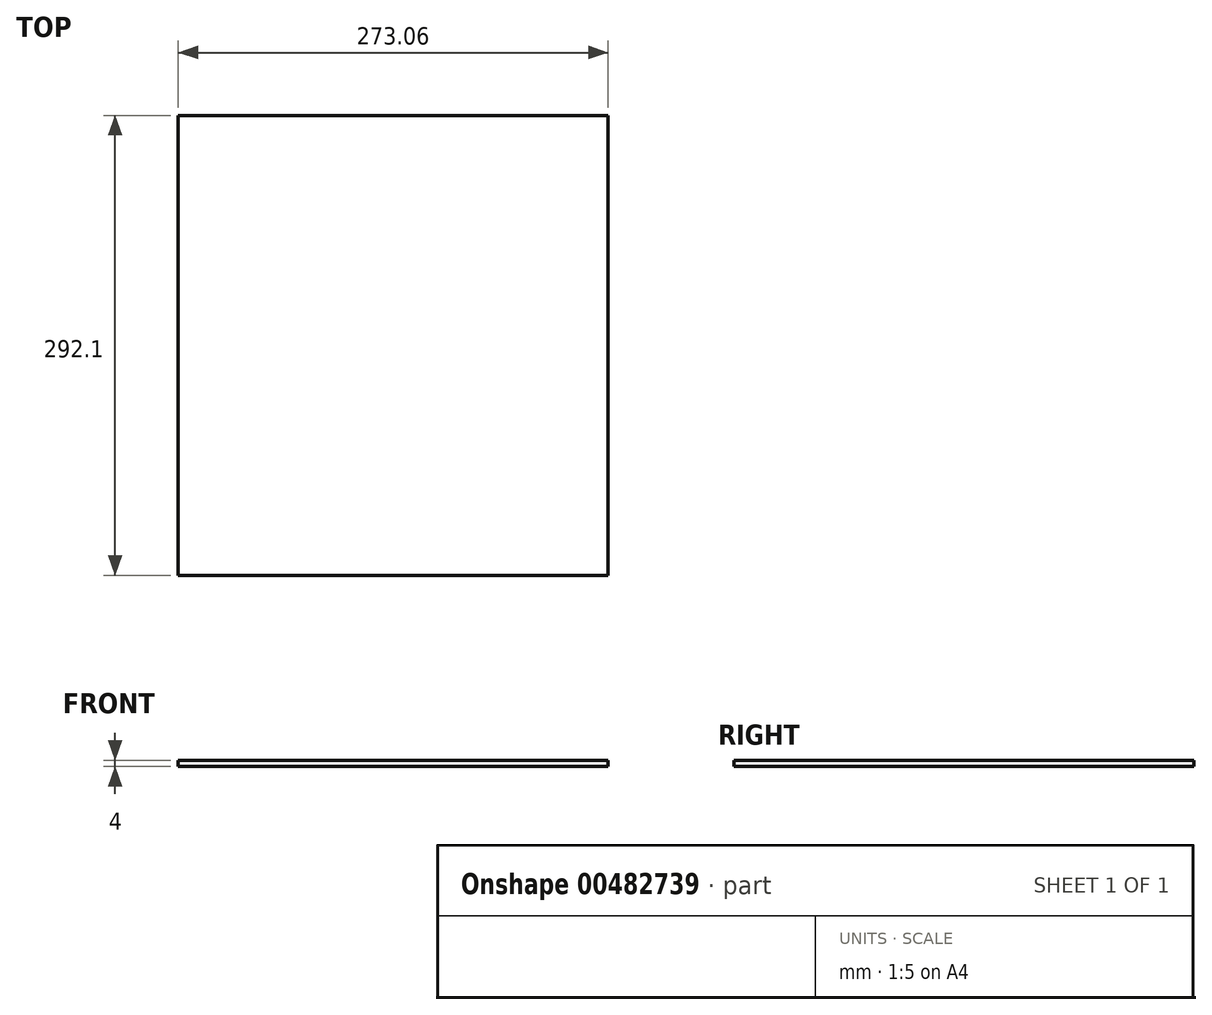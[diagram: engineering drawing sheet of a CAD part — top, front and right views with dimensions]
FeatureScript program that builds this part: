
annotation { "Feature Type Name" : "Feature", "Feature Type Description" : "" }
export const myFeature = defineFeature(function(context is Context, id is Id, definition is map)
    precondition{}
    {
        {
            var Q0;
            Q0=qCreatedBy(makeId("Top.planeOp"),FACE);
            var sketch = newSketch(context, id + "F0", { "sketchPlane" : qUnion([Q0])});
            skLineSegment(sketch, "E0.bottom", {"start": v(136.52, 146.05) * mm, "end": v(-136.53, 146.05) * mm});
            skLineSegment(sketch, "E0.top", {"start": v(136.53, -146.05) * mm, "end": v(-136.53, -146.05) * mm});
            skLineSegment(sketch, "E0.left", {"start": v(136.52, 146.05) * mm, "end": v(136.53, -146.05) * mm});
            skLineSegment(sketch, "E0.right", {"start": v(-136.53, 146.05) * mm, "end": v(-136.53, -146.05) * mm});
            skPoint(sketch, "E0.middle", {"position": v(0, 0) * mm});
            skSolve(sketch);
        }
        {
            var Q0;
            Q0=makeQuery(id+"F0.imprint","IMPRINT",FACE,{"disambiguationData":[TD([[makeQuery(id+"F0.imprint","IMPRINT",EDGE,{"derivedFrom":sQuery(id+"F0.wireOp",EDGE,"E0.bottom")}),1.0]])]});
            extrude(context, id + "F1", {"entities" : qUnion([Q0]), "depth" : 4 * mm});
        }
    });
